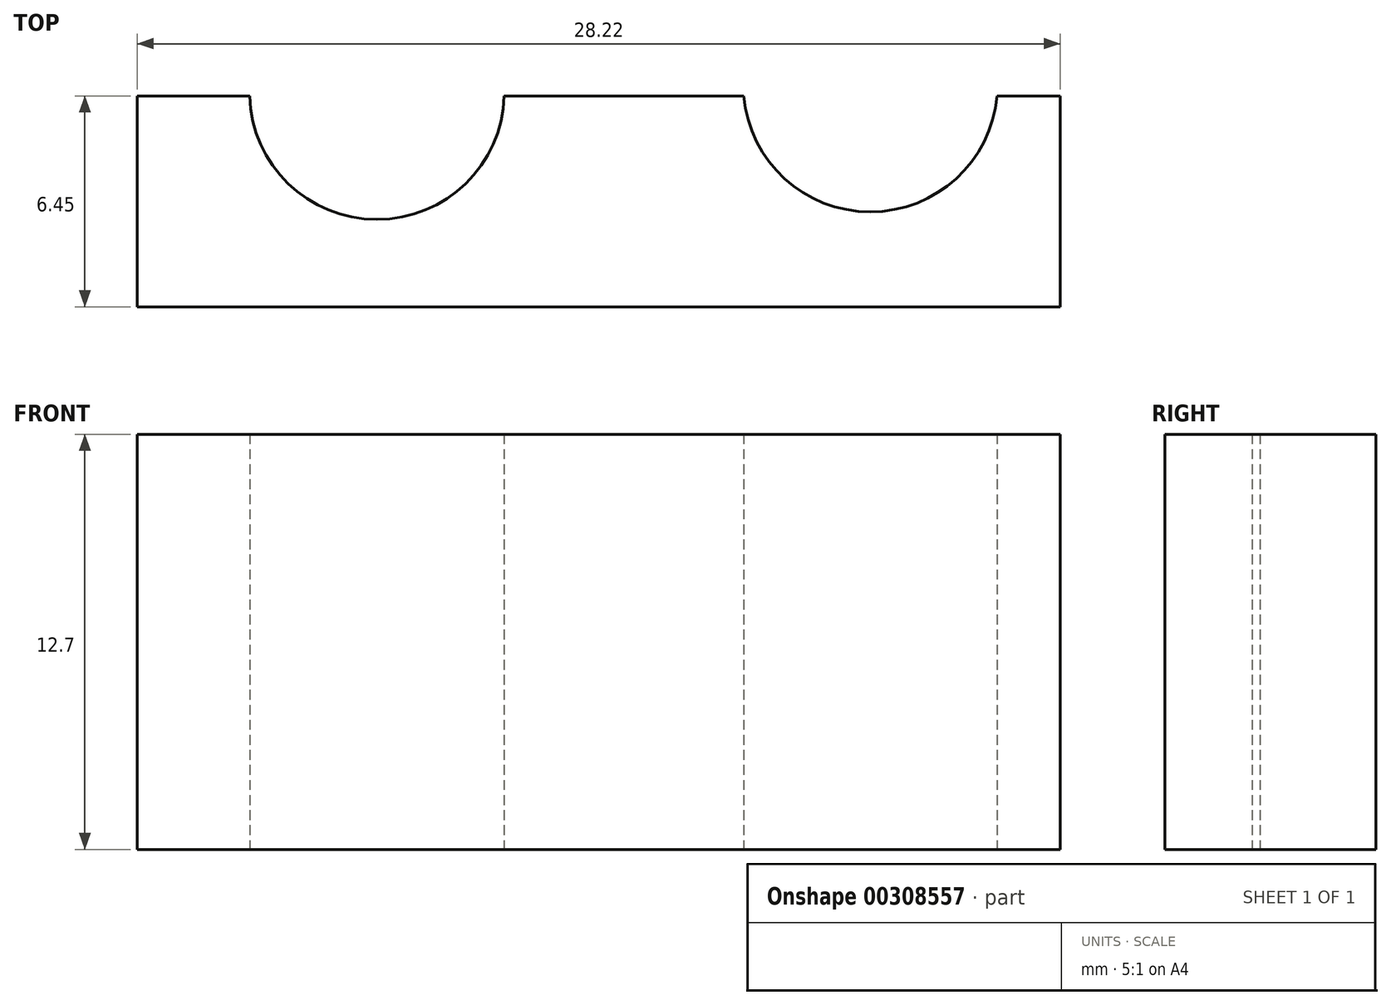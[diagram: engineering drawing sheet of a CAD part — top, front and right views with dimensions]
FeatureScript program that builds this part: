
annotation { "Feature Type Name" : "Feature", "Feature Type Description" : "" }
export const myFeature = defineFeature(function(context is Context, id is Id, definition is map)
    precondition{}
    {
        {
            var Q0;
            Q0=qCreatedBy(makeId("Top.planeOp"),FACE);
            var sketch = newSketch(context, id + "F0", { "sketchPlane" : qUnion([Q0])});
            skLineSegment(sketch, "E0", {"start": v(-11.22, 0) * mm, "end": v(17, 0) * mm});
            skLineSegment(sketch, "E1", {"start": v(17, 0) * mm, "end": v(17, 6.45) * mm});
            skLineSegment(sketch, "E2", {"start": v(17, 6.45) * mm, "end": v(15.07, 6.45) * mm});
            skArc(sketch, "E3", {"start": v(7.32, 6.45) * mm, "mid": v(11.2, 2.9) * mm, "end": v(15.07, 6.45) * mm});
            skLineSegment(sketch, "E4", {"start": v(7.32, 6.45) * mm, "end": v(0, 6.45) * mm});
            skArc(sketch, "E5", {"start": v(-7.78, 6.45) * mm, "mid": v(-3.9, 2.67) * mm, "end": v(0, 6.45) * mm});
            skLineSegment(sketch, "E6", {"start": v(-7.78, 6.45) * mm, "end": v(-11.22, 6.45) * mm});
            skLineSegment(sketch, "E7", {"start": v(-11.22, 6.45) * mm, "end": v(-11.22, 0) * mm});
            skSolve(sketch);
        }
        {
            var Q0;
            Q0=makeQuery(id+"F0.imprint","IMPRINT",FACE,{"disambiguationData":[TD([[makeQuery(id+"F0.imprint","IMPRINT",EDGE,{"derivedFrom":sQuery(id+"F0.wireOp",EDGE,"E0")}),1.0]])]});
            extrude(context, id + "F1", {"entities" : qUnion([Q0]), "depth" : 12.7 * mm});
        }
    });
